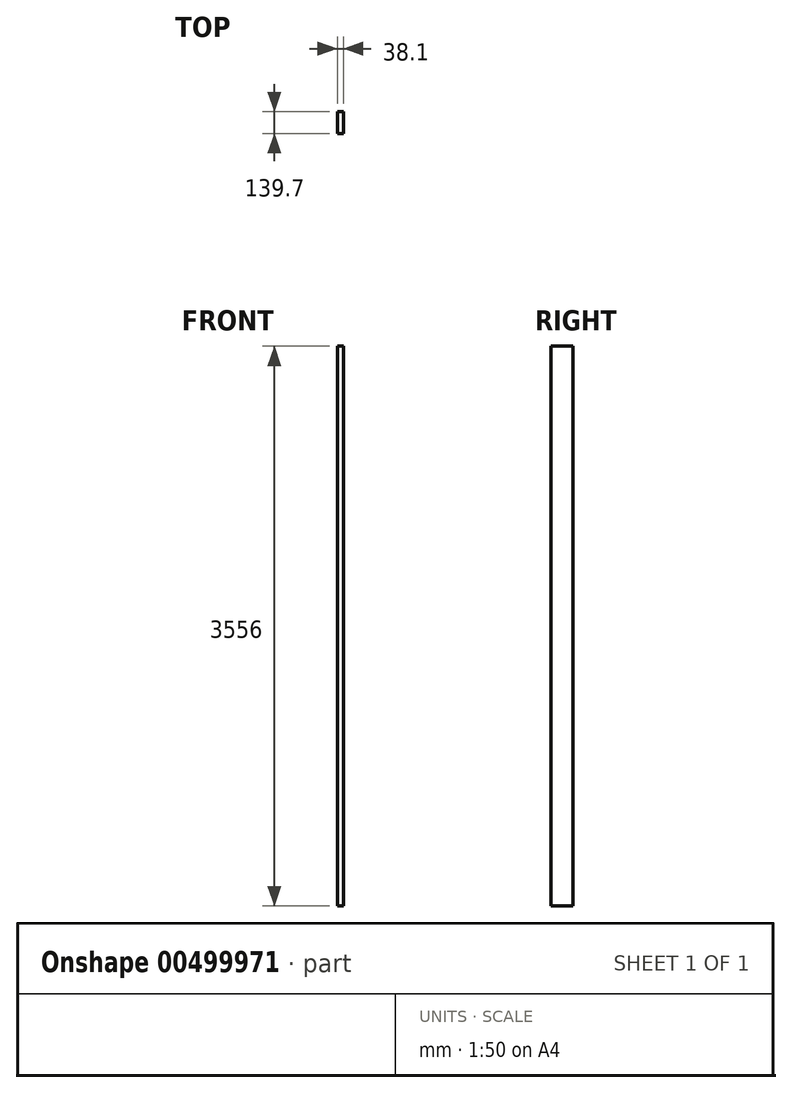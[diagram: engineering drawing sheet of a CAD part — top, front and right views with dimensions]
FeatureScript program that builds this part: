
annotation { "Feature Type Name" : "Feature", "Feature Type Description" : "" }
export const myFeature = defineFeature(function(context is Context, id is Id, definition is map)
    precondition{}
    {
        {
            var Q0;
            Q0=qCreatedBy(makeId("Right.planeOp"),FACE);
            var sketch = newSketch(context, id + "F0", { "sketchPlane" : qUnion([Q0])});
            skLineSegment(sketch, "E0.bottom", {"start": v(0, 0) * mm, "end": v(139.7, 0) * mm});
            skLineSegment(sketch, "E0.top", {"start": v(0, 3556) * mm, "end": v(139.7, 3556) * mm});
            skLineSegment(sketch, "E0.left", {"start": v(0, 0) * mm, "end": v(0, 3556) * mm});
            skLineSegment(sketch, "E0.right", {"start": v(139.7, 0) * mm, "end": v(139.7, 3556) * mm});
            skSolve(sketch);
        }
        {
            var Q0;
            Q0 = qSketchRegion(id + "F0", true);
            extrude(context, id + "F1", {"entities" : qUnion([Q0]), "depth" : 38.1 * mm, "offsetDistance" : 25.4 * mm});
        }
    });
